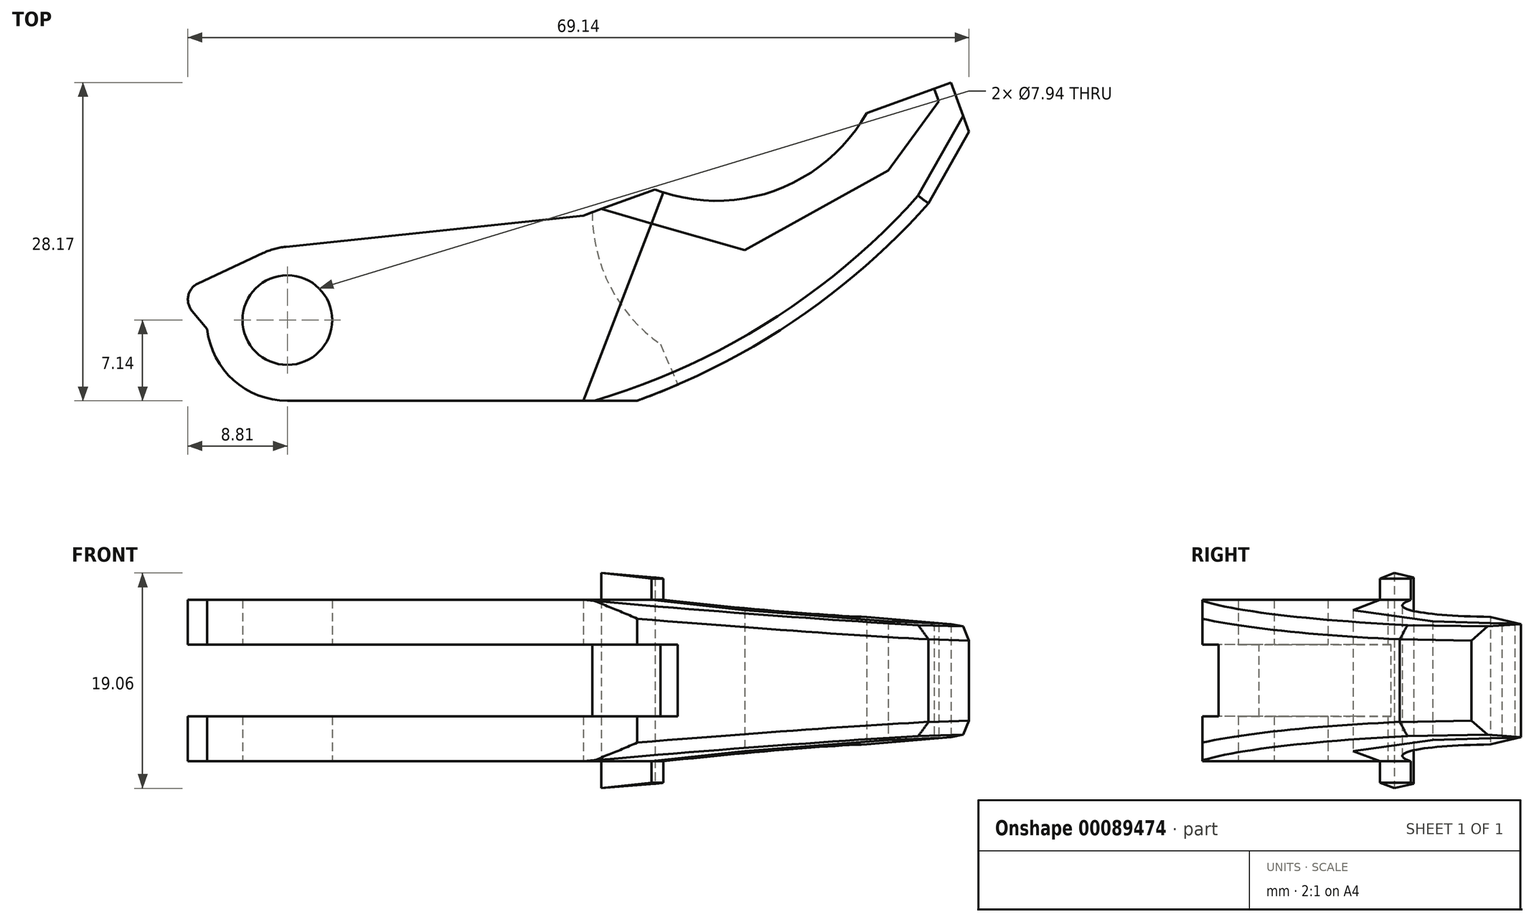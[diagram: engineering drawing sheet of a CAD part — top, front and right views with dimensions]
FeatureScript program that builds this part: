
annotation { "Feature Type Name" : "Feature", "Feature Type Description" : "" }
export const myFeature = defineFeature(function(context is Context, id is Id, definition is map)
    precondition{}
    {
        {
            var Q0;
            Q0=qCreatedBy(makeId("Top.planeOp"),FACE);
            var sketch = newSketch(context, id + "F0", { "sketchPlane" : qUnion([Q0])});
            skCircle(sketch, "E0", {"center": v(0, 0) * mm, "radius": 3.97 * mm});
            skLineSegment(sketch, "E1", {"start": v(30.96, -7.14) * mm, "end": v(0, -7.14) * mm});
            skArc(sketch, "E2", {"start": v(-7.1, -0.8) * mm, "mid": v(-4.76, -5.32) * mm, "end": v(0, -7.14) * mm});
            skLineSegment(sketch, "E3", {"start": v(-7.1, -0.8) * mm, "end": v(-8.43, 0.8) * mm});
            skLineSegment(sketch, "E4", {"start": v(-7.89, 3.26) * mm, "end": v(-1.2, 6.38) * mm});
            skLineSegment(sketch, "E5", {"start": v(-1.2, 6.38) * mm, "end": v(26.2, 9.26) * mm});
            skLineSegment(sketch, "E6", {"start": v(26.2, 9.26) * mm, "end": v(58.75, 21.03) * mm});
            skLineSegment(sketch, "E7", {"start": v(58.75, 21.03) * mm, "end": v(60.33, 16.67) * mm});
            skLineSegment(sketch, "E8", {"start": v(60.33, 16.67) * mm, "end": v(56.75, 10.32) * mm});
            skArc(sketch, "E9", {"start": v(30.96, -7.14) * mm, "mid": v(44.94, -0.02) * mm, "end": v(56.75, 10.32) * mm});
            skLineSegment(sketch, "E10", {"start": v(26.2, -7.14) * mm, "end": v(33.5, 11.9) * mm, "construction": true});
            skLineSegment(sketch, "E11", {"start": v(40.48, 6.19) * mm, "end": v(53.18, 13.23) * mm});
            skLineSegment(sketch, "E12", {"start": v(53.18, 13.23) * mm, "end": v(57.66, 19.37) * mm});
            skLineSegment(sketch, "E13", {"start": v(57.66, 19.37) * mm, "end": v(57.25, 20.5) * mm});
            skLineSegment(sketch, "E14", {"start": v(40.48, 6.19) * mm, "end": v(27.78, 9.83) * mm});
            skArc(sketch, "E15", {"start": v(32.54, 11.55) * mm, "mid": v(43.17, 11.46) * mm, "end": v(51.28, 18.33) * mm});
            skPoint(sketch, "E16.visualSharp", {"position": v(-9.76, 2.38) * mm});
            skArc(sketch, "E16.filletArc", {"start": v(-7.89, 3.26) * mm, "mid": v(-8.77, 2.16) * mm, "end": v(-8.43, 0.8) * mm});
            skSolve(sketch);
        }
        {
            var Q0;
            Q0=makeQuery(id+"F0.imprint","IMPRINT",FACE,{"disambiguationData":[TD([[makeQuery(id+"F0.imprint","IMPRINT",EDGE,{"derivedFrom":sQuery(id+"F0.wireOp",EDGE,"E0")}),-1.0]])]});
            extrude(context, id + "F1", {"entities" : qUnion([Q0]), "endBound" : BoundingType.SYMMETRIC, "depth" : 14.29 * mm});
        }
        {
            var Q0;
            Q0=makeQuery(id+"F0.imprint","IMPRINT",FACE,{"disambiguationData":[TD([[makeQuery(id+"F0.imprint","IMPRINT",EDGE,{"derivedFrom":sQuery(id+"F0.wireOp",EDGE,"E11")}),1.0]])]});
            extrude(context, id + "F2", {"entities" : qUnion([Q0]), "endBound" : BoundingType.SYMMETRIC, "depth" : 19.05 * mm});
        }
        {
            var Q0;
            Q0=makeQuery(id+"F1.opExtrude","SWEPT_EDGE",EDGE,{"disambiguationData":[OSD([sQuery(id+"F0.wireOp",EDGE,"E4"),sQuery(id+"F0.wireOp",EDGE,"E5")])]});
            fillet(context, id + "F3", {"entities" : qUnion([Q0]), "radius" : 6.35 * mm, "tangentPropagation" : true, "allowEdgeOverflow" : false});
        }
        {
            var Q0;
            Q0=sQuery(id+"F0.wireOp",EDGE,"E10");
            var Q1;
            Q1=sQuery(id+"F0.wireOp",VERTEX,"E10.start");
            cPlane(context, id + "F4", {"entities" : qUnion([Q0, Q1]), "cplaneType" : CPlaneType.LINE_POINT, "offset" : 152.4 * mm, "width" : 152.4 * mm, "height" : 152.4 * mm});
        }
        {
            var Q0;
            Q0=qCreatedBy(id+"F4.planeOp",FACE);
            var sketch = newSketch(context, id + "F5", { "sketchPlane" : qUnion([Q0])});
            skLineSegment(sketch, "E17.0", {"start": v(-35.57, 9.53) * mm, "end": v(-22.41, 9.53) * mm, "construction": true});
            skLineSegment(sketch, "E18.0", {"start": v(-31.46, 7.14) * mm, "end": v(-2.56, 7.14) * mm, "construction": true});
            skLineSegment(sketch, "E19", {"start": v(-22.41, 9.53) * mm, "end": v(-61.69, 5.4) * mm});
            skLineSegment(sketch, "E20", {"start": v(-27.01, 7.14) * mm, "end": v(-68.08, 2.83) * mm});
            skPoint(sketch, "E21.0", {"position": v(-27.01, 0) * mm});
            skLineSegment(sketch, "E22", {"start": v(-27.01, 0) * mm, "end": v(-27.01, 11.67) * mm, "construction": true});
            skLineSegment(sketch, "E23", {"start": v(-22.41, 9.53) * mm, "end": v(-22.41, 22.94) * mm});
            skLineSegment(sketch, "E24", {"start": v(-22.41, 22.94) * mm, "end": v(-61.69, 22.94) * mm});
            skLineSegment(sketch, "E25", {"start": v(-61.69, 22.94) * mm, "end": v(-61.69, 5.4) * mm});
            skLineSegment(sketch, "E26", {"start": v(-68.08, 2.83) * mm, "end": v(-68.08, 14.14) * mm});
            skLineSegment(sketch, "E27", {"start": v(-68.08, 14.14) * mm, "end": v(-27.01, 14.14) * mm});
            skLineSegment(sketch, "E28", {"start": v(-27.01, 14.14) * mm, "end": v(-27.01, 7.14) * mm});
            skLineSegment(sketch, "E29.MirrorCS", {"start": v(-22.41, -9.53) * mm, "end": v(-22.41, -22.94) * mm});
            skLineSegment(sketch, "E30.MirrorCS", {"start": v(-22.41, -22.94) * mm, "end": v(-61.69, -22.94) * mm});
            skLineSegment(sketch, "E31.MirrorCS", {"start": v(-68.08, -14.14) * mm, "end": v(-27.01, -14.14) * mm});
            skLineSegment(sketch, "E32.MirrorCS", {"start": v(-61.69, -22.94) * mm, "end": v(-61.69, -5.4) * mm});
            skLineSegment(sketch, "E33.MirrorCS", {"start": v(-68.08, -2.83) * mm, "end": v(-68.08, -14.14) * mm});
            skLineSegment(sketch, "E34.MirrorCS", {"start": v(-27.01, -7.14) * mm, "end": v(-68.08, -2.83) * mm});
            skLineSegment(sketch, "E35.MirrorCS", {"start": v(-27.01, 0) * mm, "end": v(-27.01, -11.67) * mm, "construction": true});
            skLineSegment(sketch, "E36.MirrorCS", {"start": v(-27.01, -14.14) * mm, "end": v(-27.01, -7.14) * mm});
            skLineSegment(sketch, "E37.MirrorCS", {"start": v(-22.41, -9.53) * mm, "end": v(-61.69, -5.4) * mm});
            skSolve(sketch);
        }
        {
            var Q0;
            {var subQ4=sQuery(id+"F5.wireOp",EDGE,"E23");Q0=makeQuery(id+"F5.imprint","IMPRINT",FACE,{"disambiguationData":[TD([[makeQuery(id+"F5.imprint","IMPRINT",EDGE,{"derivedFrom":subQ4}),1.0]])]});}
            var Q1;
            {var subQ0=sQuery(id+"F5.wireOp",EDGE,"E25");var subQ1=sQuery(id+"F5.wireOp",EDGE,"E19");var subQ2=makeQuery(id+"F5.imprint","INTERSECT",VERTEX,{"derivedFrom":[subQ1,subQ0]});Q1=makeQuery(id+"F5.imprint","IMPRINT",FACE,{"disambiguationData":[TD([[makeQuery(id+"F5.imprint","IMPRINT",EDGE,{"disambiguationData":[TD([[subQ2,1.0]])],"derivedFrom":subQ1}),-1.0]])]});}
            var Q2;
            {var subQ6=sQuery(id+"F5.wireOp",EDGE,"E29.MirrorCS");Q2=makeQuery(id+"F5.imprint","IMPRINT",FACE,{"disambiguationData":[TD([[makeQuery(id+"F5.imprint","IMPRINT",EDGE,{"derivedFrom":subQ6}),-1.0]])]});}
            var Q3;
            {var subQ0=sQuery(id+"F5.wireOp",EDGE,"E36.MirrorCS");var subQ1=sQuery(id+"F5.wireOp",EDGE,"E31.MirrorCS");var subQ2=makeQuery(id+"F5.imprint","INTERSECT",VERTEX,{"derivedFrom":[subQ1,subQ0]});Q3=makeQuery(id+"F5.imprint","IMPRINT",FACE,{"disambiguationData":[TD([[makeQuery(id+"F5.imprint","IMPRINT",EDGE,{"disambiguationData":[TD([[subQ2,1.0]])],"derivedFrom":subQ1}),1.0]])]});}
            extrude(context, id + "F6", {"entities" : qUnion([Q0, Q1, Q2, Q3]), "operationType" : NewBodyOperationType.REMOVE, "depth" : 51.3 * mm});
        }
        {
            var Q0;
            {var subQ6=sQuery(id+"F5.wireOp",EDGE,"E20");Q0=makeQuery(id+"F5.imprint","IMPRINT",FACE,{"disambiguationData":[TD([[makeQuery(id+"F5.imprint","IMPRINT",EDGE,{"derivedFrom":subQ6}),-1.0]])]});}
            var Q1;
            {var subQ0=sQuery(id+"F5.wireOp",EDGE,"E25");var subQ1=sQuery(id+"F5.wireOp",EDGE,"E19");var subQ2=makeQuery(id+"F5.imprint","INTERSECT",VERTEX,{"derivedFrom":[subQ1,subQ0]});Q1=makeQuery(id+"F5.imprint","IMPRINT",FACE,{"disambiguationData":[TD([[makeQuery(id+"F5.imprint","IMPRINT",EDGE,{"disambiguationData":[TD([[subQ2,1.0]])],"derivedFrom":subQ1}),-1.0]])]});}
            var Q2;
            {var subQ0=sQuery(id+"F5.wireOp",EDGE,"E33.MirrorCS");Q2=makeQuery(id+"F5.imprint","IMPRINT",FACE,{"disambiguationData":[TD([[makeQuery(id+"F5.imprint","IMPRINT",EDGE,{"derivedFrom":subQ0}),1.0]])]});}
            var Q3;
            {var subQ0=sQuery(id+"F5.wireOp",EDGE,"E36.MirrorCS");var subQ1=sQuery(id+"F5.wireOp",EDGE,"E31.MirrorCS");var subQ2=makeQuery(id+"F5.imprint","INTERSECT",VERTEX,{"derivedFrom":[subQ1,subQ0]});Q3=makeQuery(id+"F5.imprint","IMPRINT",FACE,{"disambiguationData":[TD([[makeQuery(id+"F5.imprint","IMPRINT",EDGE,{"disambiguationData":[TD([[subQ2,1.0]])],"derivedFrom":subQ1}),1.0]])]});}
            extrude(context, id + "F7", {"entities" : qUnion([Q0, Q1, Q2, Q3]), "operationType" : NewBodyOperationType.REMOVE, "depth" : 54.25 * mm});
        }
        {
            var Q0;
            Q0=qCreatedBy(makeId("Top.planeOp"),FACE);
            var sketch = newSketch(context, id + "F8", { "sketchPlane" : qUnion([Q0])});
            skArc(sketch, "E38", {"start": v(27.8, 14.26) * mm, "mid": v(27.66, 5.19) * mm, "end": v(33.02, -2.14) * mm});
            skLineSegment(sketch, "E39", {"start": v(33.02, -2.14) * mm, "end": v(37.87, -13.35) * mm});
            skLineSegment(sketch, "E40", {"start": v(27.8, 14.26) * mm, "end": v(-12.56, 14.26) * mm});
            skLineSegment(sketch, "E41", {"start": v(-12.56, 14.26) * mm, "end": v(-12.56, -13.35) * mm});
            skLineSegment(sketch, "E42", {"start": v(-12.56, -13.35) * mm, "end": v(37.87, -13.35) * mm});
            skSolve(sketch);
        }
        {
            var Q0;
            Q0=makeQuery(id+"F8.imprint","IMPRINT",FACE,{"disambiguationData":[TD([[makeQuery(id+"F8.imprint","IMPRINT",EDGE,{"derivedFrom":sQuery(id+"F8.wireOp",EDGE,"E38")}),-1.0]])]});
            extrude(context, id + "F9", {"entities" : qUnion([Q0]), "operationType" : NewBodyOperationType.REMOVE, "endBound" : BoundingType.SYMMETRIC, "oppositeDirection" : true, "depth" : 6.35 * mm});
        }
        {
            var Q0;
            Q0=makeQuery(id+"F7.boolean.opBoolean","INTERSECT",EDGE,{"derivedFrom":[makeQuery(id+"F1.opExtrude","SWEPT_FACE",FACE,{"disambiguationData":[OSD([sQuery(id+"F0.wireOp",EDGE,"E9")])]}),makeQuery(id+"F7.opExtrude","SWEPT_FACE",FACE,{"disambiguationData":[OSD([sQuery(id+"F5.wireOp",EDGE,"E20")])]})]});
            var Q1;
            Q1=makeQuery(id+"F7.boolean.opBoolean","INTERSECT",EDGE,{"derivedFrom":[makeQuery(id+"F1.opExtrude","SWEPT_FACE",FACE,{"disambiguationData":[OSD([sQuery(id+"F0.wireOp",EDGE,"E8")])]}),makeQuery(id+"F7.opExtrude","SWEPT_FACE",FACE,{"disambiguationData":[OSD([sQuery(id+"F5.wireOp",EDGE,"E20")])]})]});
            var Q2;
            Q2=makeQuery(id+"F7.boolean.opBoolean","INTERSECT",EDGE,{"derivedFrom":[makeQuery(id+"F1.opExtrude","SWEPT_FACE",FACE,{"disambiguationData":[OSD([sQuery(id+"F0.wireOp",EDGE,"E9")])]}),makeQuery(id+"F7.opExtrude","SWEPT_FACE",FACE,{"disambiguationData":[OSD([sQuery(id+"F5.wireOp",EDGE,"E34.MirrorCS")])]})]});
            var Q3;
            Q3=makeQuery(id+"F7.boolean.opBoolean","INTERSECT",EDGE,{"derivedFrom":[makeQuery(id+"F1.opExtrude","SWEPT_FACE",FACE,{"disambiguationData":[OSD([sQuery(id+"F0.wireOp",EDGE,"E8")])]}),makeQuery(id+"F7.opExtrude","SWEPT_FACE",FACE,{"disambiguationData":[OSD([sQuery(id+"F5.wireOp",EDGE,"E34.MirrorCS")])]})]});
            chamfer(context, id + "F10", {"entities" : qUnion([Q0, Q1, Q2, Q3]), "width" : 1.27 * mm, "tangentPropagation" : true});
        }
    });
